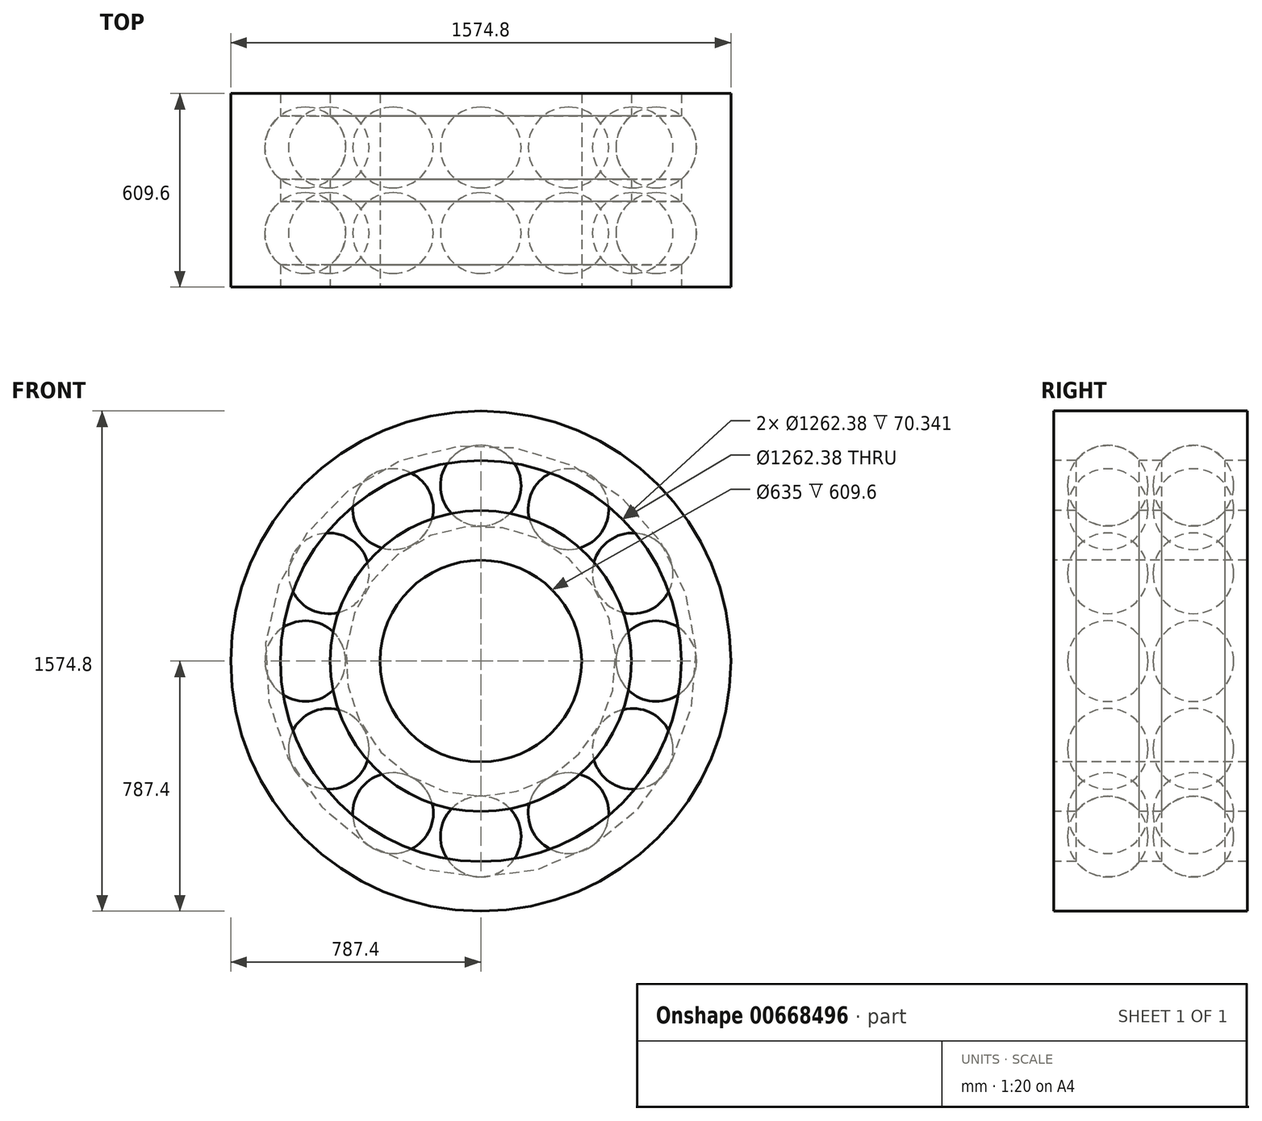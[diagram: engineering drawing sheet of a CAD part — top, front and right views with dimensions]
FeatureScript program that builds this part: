
annotation { "Feature Type Name" : "Feature", "Feature Type Description" : "" }
export const myFeature = defineFeature(function(context is Context, id is Id, definition is map)
    precondition{}
    {
        {
            var Q0;
            Q0=qCreatedBy(makeId("Right.planeOp"),FACE);
            var sketch = newSketch(context, id + "F0", { "sketchPlane" : qUnion([Q0])});
            skLineSegment(sketch, "E0.bottom", {"start": v(-304.8, 631.2) * mm, "end": v(-234.46, 631.2) * mm});
            skLineSegment(sketch, "E0.top", {"start": v(-304.8, 787.4) * mm, "end": v(304.8, 787.4) * mm});
            skLineSegment(sketch, "E0.left", {"start": v(-304.8, 631.2) * mm, "end": v(-304.8, 787.4) * mm});
            skLineSegment(sketch, "E0.right", {"start": v(304.8, 631.2) * mm, "end": v(304.8, 787.4) * mm});
            skLineSegment(sketch, "E1.bottom", {"start": v(-304.8, 473.71) * mm, "end": v(-234.46, 473.71) * mm});
            skLineSegment(sketch, "E1.top", {"start": v(-304.8, 317.5) * mm, "end": v(304.8, 317.5) * mm});
            skLineSegment(sketch, "E1.left", {"start": v(-304.8, 473.71) * mm, "end": v(-304.8, 317.5) * mm});
            skLineSegment(sketch, "E1.right", {"start": v(304.8, 473.71) * mm, "end": v(304.8, 317.5) * mm});
            skLineSegment(sketch, "E2", {"start": v(-1154.66, 0) * mm, "end": v(1193.5, 0) * mm, "construction": true});
            skLineSegment(sketch, "E3", {"start": v(-304.8, 552.45) * mm, "end": v(304.8, 552.45) * mm, "construction": true});
            skArc(sketch, "E4", {"start": v(-234.46, 473.7) * mm, "mid": v(-134.81, 425.45) * mm, "end": v(-35.17, 473.71) * mm});
            skLineSegment(sketch, "E5", {"start": v(0, 787.4) * mm, "end": v(0, -1078.57) * mm, "construction": true});
            skLineSegment(sketch, "E6.trimOffspring", {"start": v(-35.17, 631.2) * mm, "end": v(35.17, 631.2) * mm});
            skLineSegment(sketch, "E7.trimOffspring", {"start": v(-35.17, 473.71) * mm, "end": v(35.17, 473.71) * mm});
            skArc(sketch, "E8.trimOffspring", {"start": v(-35.17, 631.2) * mm, "mid": v(-134.81, 679.45) * mm, "end": v(-234.46, 631.2) * mm});
            skArc(sketch, "E9", {"start": v(35.17, 473.71) * mm, "mid": v(134.81, 425.45) * mm, "end": v(234.46, 473.7) * mm});
            skLineSegment(sketch, "E10.trimOffspring", {"start": v(234.46, 631.2) * mm, "end": v(304.8, 631.2) * mm});
            skLineSegment(sketch, "E11.trimOffspring", {"start": v(234.46, 473.71) * mm, "end": v(304.8, 473.71) * mm});
            skArc(sketch, "E12.trimOffspring", {"start": v(234.46, 631.2) * mm, "mid": v(134.81, 679.45) * mm, "end": v(35.17, 631.2) * mm});
            skLineSegment(sketch, "E13.bottom", {"start": v(-134.81, 617.41) * mm, "end": v(134.81, 617.41) * mm, "construction": true});
            skLineSegment(sketch, "E13.top", {"start": v(-134.81, 487.49) * mm, "end": v(134.81, 487.49) * mm, "construction": true});
            skLineSegment(sketch, "E13.left", {"start": v(-134.81, 617.41) * mm, "end": v(-134.81, 487.49) * mm, "construction": true});
            skLineSegment(sketch, "E13.right", {"start": v(134.81, 617.41) * mm, "end": v(134.81, 487.49) * mm, "construction": true});
            skLineSegment(sketch, "E14", {"start": v(-304.8, 787.4) * mm, "end": v(-134.81, 617.41) * mm, "construction": true});
            skSolve(sketch);
        }
        {
            var Q0;
            Q0=qCreatedBy(makeId("Right.planeOp"),FACE);
            var sketch = newSketch(context, id + "F1", { "sketchPlane" : qUnion([Q0])});
            skPoint(sketch, "E15.0", {"position": v(-134.81, 552.45) * mm});
            skLineSegment(sketch, "E16.0", {"start": v(-304.8, 552.45) * mm, "end": v(304.8, 552.45) * mm, "construction": true});
            skPoint(sketch, "E17.0", {"position": v(134.81, 552.45) * mm});
            skArc(sketch, "E18", {"start": v(-7.81, 552.45) * mm, "mid": v(-134.81, 679.45) * mm, "end": v(-261.81, 552.45) * mm});
            skArc(sketch, "E19", {"start": v(261.81, 552.45) * mm, "mid": v(134.81, 679.45) * mm, "end": v(7.81, 552.45) * mm});
            skLineSegment(sketch, "E20", {"start": v(-261.81, 552.45) * mm, "end": v(-7.81, 552.45) * mm});
            skLineSegment(sketch, "E21", {"start": v(7.81, 552.45) * mm, "end": v(261.81, 552.45) * mm});
            skSolve(sketch);
        }
        {
            var Q0;
            Q0=makeQuery(id+"F1.imprint","IMPRINT",FACE,{"disambiguationData":[TD([[makeQuery(id+"F1.imprint","IMPRINT",EDGE,{"derivedFrom":sQuery(id+"F1.wireOp",EDGE,"E18")}),1.0]])]});
            var Q1;
            Q1=makeQuery(id+"F1.imprint","IMPRINT",FACE,{"disambiguationData":[TD([[makeQuery(id+"F1.imprint","IMPRINT",EDGE,{"derivedFrom":sQuery(id+"F1.wireOp",EDGE,"E19")}),1.0]])]});
            var Q2;
            Q2=sQuery(id+"F1.wireOp",EDGE,"E20");
            revolve(context, id + "F2", {"entities" : qUnion([Q0, Q1]), "axis" : qUnion([Q2]), "revolveType" : RevolveType.FULL});
        }
        {
            var Q0;
            {var subQ4=sQuery(id+"F0.wireOp",EDGE,"E0.bottom");Q0=makeQuery(id+"F0.imprint","IMPRINT",FACE,{"disambiguationData":[TD([[makeQuery(id+"F0.imprint","IMPRINT",EDGE,{"derivedFrom":subQ4}),1.0]])]});}
            var Q1;
            {var subQ2=sQuery(id+"F0.wireOp",EDGE,"E1.bottom");Q1=makeQuery(id+"F0.imprint","IMPRINT",FACE,{"disambiguationData":[TD([[makeQuery(id+"F0.imprint","IMPRINT",EDGE,{"derivedFrom":subQ2}),-1.0]])]});}
            var Q2;
            Q2=sQuery(id+"F0.wireOp",EDGE,"E2");
            revolve(context, id + "F3", {"entities" : qUnion([Q0, Q1]), "axis" : qUnion([Q2]), "revolveType" : RevolveType.FULL});
        }
        {
            var Q0;
            Q0=makeQuery(id+"F2.opRevolve","SWEPT_BODY",BODY,{"disambiguationData":[OSD([sQuery(id+"F1.wireOp",EDGE,"E18"),sQuery(id+"F1.wireOp",EDGE,"E20")])]});
            var Q1;
            Q1=makeQuery(id+"F2.opRevolve","SWEPT_BODY",BODY,{"disambiguationData":[OSD([sQuery(id+"F1.wireOp",EDGE,"E19"),sQuery(id+"F1.wireOp",EDGE,"E21")])]});
            var Q2;
            Q2=sQuery(id+"F0.wireOp",EDGE,"E2");
            circularPattern(context, id + "F4", {"entities" : qUnion([Q0, Q1]), "axis" : qUnion([Q2]), "angle" : 30 * degree, "instanceCount" : 12});
        }
    });
